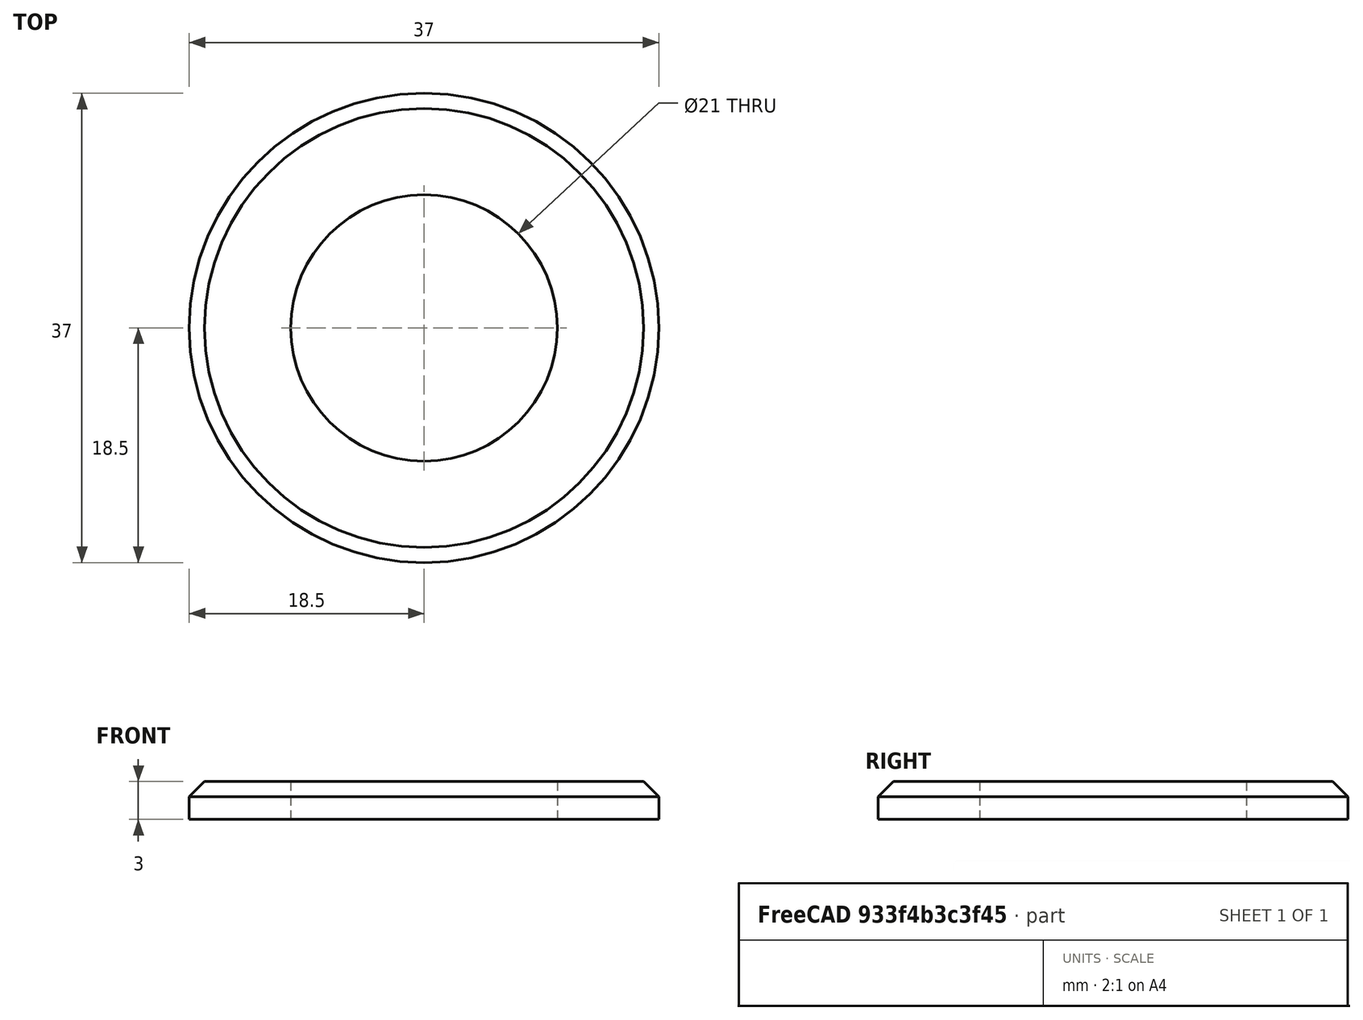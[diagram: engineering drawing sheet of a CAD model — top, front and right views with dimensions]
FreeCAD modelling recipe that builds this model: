
FCSTD DOCUMENT  (FreeCAD 0.15R4651 (Git))
Label: Scheibe_DIN125-B 21
License: CC-BY 3.0
LicenseURL: http://creativecommons.org/licenses/by/3.0/
objects: Sketcher::SketchObject×1, PartDesign::Revolution×1
note: 3 computed .brp shape members not serialized (recipe doc carries the construction recipe); baked Part::Feature solids carry a one-line shape summary decoded from their .brp

FEATURE [Sketcher::SketchObject] Sketch
  Placement = pos=(0,0,0) rot=(0.57735,0.57735,0.57735;2.0944rad)
  sketch-geometry (5):
    g0: LineSegment StartX=10.5 StartY=0 StartZ=0 EndX=18.5 EndY=0 EndZ=0
    g1: LineSegment StartX=18.5 StartY=0 StartZ=0 EndX=18.5 EndY=1.8 EndZ=0
    g2: LineSegment StartX=17.3 StartY=3 StartZ=0 EndX=10.5 EndY=3 EndZ=0
    g3: LineSegment StartX=10.5 StartY=3 StartZ=0 EndX=10.5 EndY=0 EndZ=0
    g4: LineSegment StartX=17.3 StartY=3 StartZ=0 EndX=18.5 EndY=1.8 EndZ=0
  constraints (15):
    c: Coincident(g0,g1)
    c: Coincident(g2,g3)
    c: Coincident(g3,g0)
    c: Horizontal(g0)
    c: Horizontal(g2)
    c: Vertical(g1)
    c: Vertical(g3)
    c: PointOnObject(g0,g-1)
    c: DistanceX(g-1,g2) = 10.5
    c: Coincident(g1,g4)
    c: Coincident(g2,g4)
    c: DistanceY(g3) = -3
    c: DistanceX(g-1,g1) = 18.5
    c: DistanceX(g4) = 1.2
    c: DistanceY(g4) = -1.2
FEATURE [PartDesign::Revolution] Revolution  label="Scheibe DIN 125 - B 21 #"
  Angle = 360
  Axis = (0,0,1)
  Base = (0,0,0)
  Placement = pos=(0,0,0) rot=(0.57735,0.57735,0.57735;2.0944rad)
  ReferenceAxis = -> Sketch [V_Axis]
  Reversed = true
  Sketch = -> Sketch
